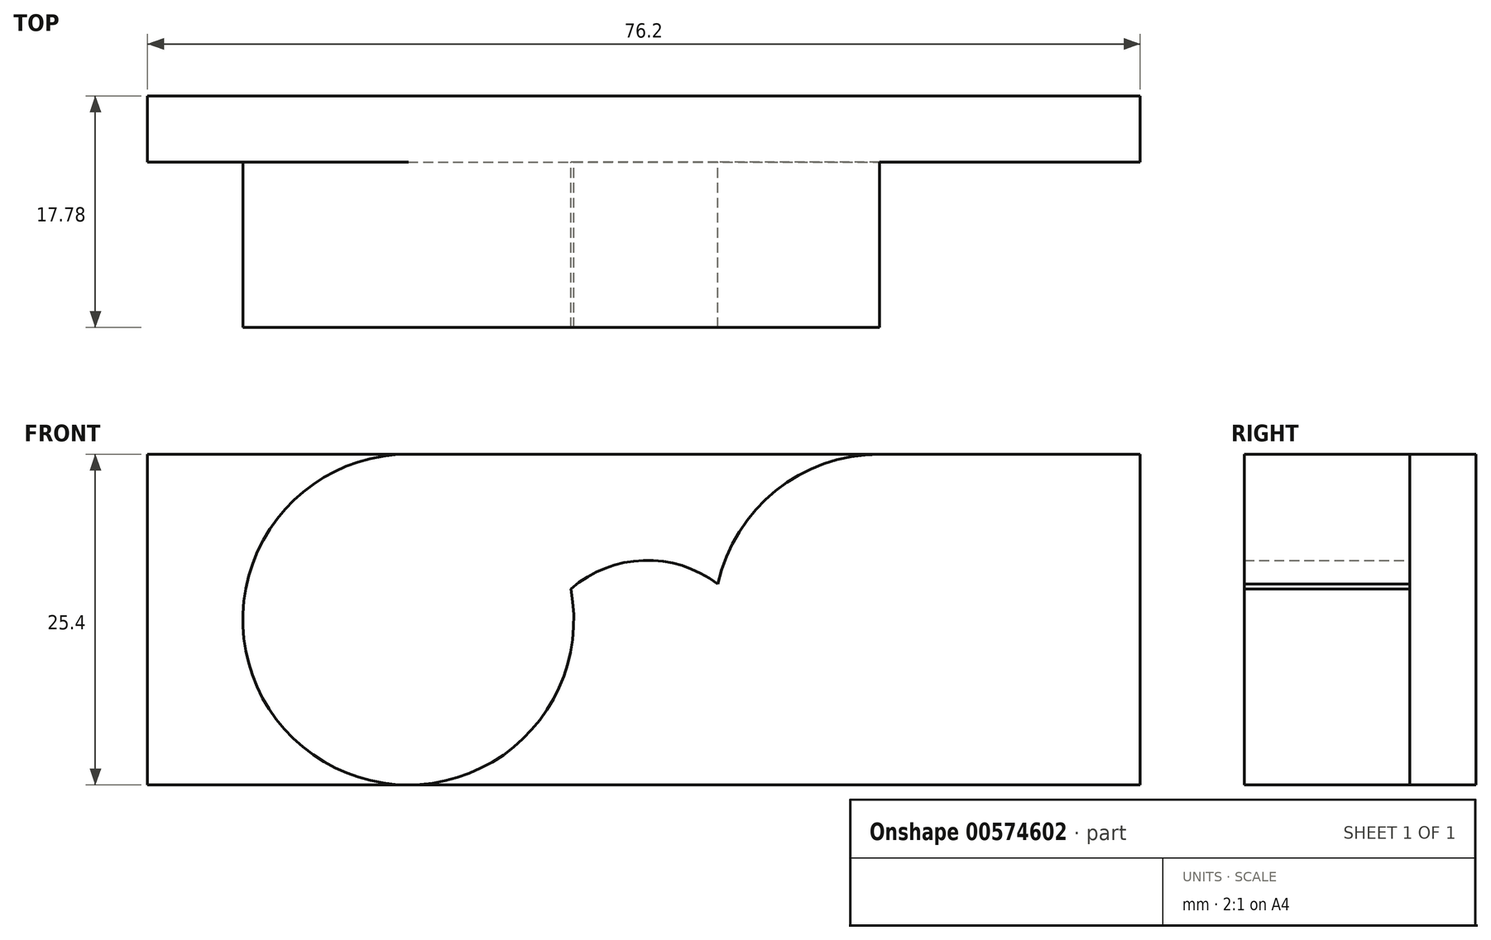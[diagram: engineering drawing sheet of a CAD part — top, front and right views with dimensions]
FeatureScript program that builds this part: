
annotation { "Feature Type Name" : "Feature", "Feature Type Description" : "" }
export const myFeature = defineFeature(function(context is Context, id is Id, definition is map)
    precondition{}
    {
        {
            var Q0;
            Q0=qCreatedBy(makeId("Front.planeOp"),FACE);
            var sketch = newSketch(context, id + "F0", { "sketchPlane" : qUnion([Q0])});
            skLineSegment(sketch, "E0.bottom", {"start": v(-38.1, 12.7) * mm, "end": v(38.1, 12.7) * mm});
            skLineSegment(sketch, "E0.top", {"start": v(-38.1, -12.7) * mm, "end": v(38.1, -12.7) * mm});
            skLineSegment(sketch, "E0.left", {"start": v(-38.1, 12.7) * mm, "end": v(-38.1, -12.7) * mm});
            skLineSegment(sketch, "E0.right", {"start": v(38.1, 12.7) * mm, "end": v(38.1, -12.7) * mm});
            skSolve(sketch);
        }
        {
            var Q0;
            Q0 = qSketchRegion(id + "F0", true);
            extrude(context, id + "F1", {"entities" : qUnion([Q0]), "depth" : 5.08 * mm, "offsetDistance" : 25.4 * mm});
        }
        {
            var Q0;
            Q0=makeQuery(id+"F1.opExtrude","CAP_FACE",FACE,{"disambiguationData":[OSD([sQuery(id+"F0.wireOp",EDGE,"E0.bottom"),sQuery(id+"F0.wireOp",EDGE,"E0.top"),sQuery(id+"F0.wireOp",EDGE,"E0.left"),sQuery(id+"F0.wireOp",EDGE,"E0.right")])],"isStart":false});
            var sketch = newSketch(context, id + "F2", { "sketchPlane" : qUnion([Q0])});
            skCircle(sketch, "E1", {"center": v(-18.08, 0) * mm, "radius": 12.7 * mm});
            skCircle(sketch, "E2.MirrorC", {"center": v(18.08, 0) * mm, "radius": 12.7 * mm});
            skArc(sketch, "E3", {"start": v(6.12, 4.27) * mm, "mid": v(0, 6.38) * mm, "end": v(-6.02, 3.98) * mm});
            skArc(sketch, "E4", {"start": v(5.68, 2.74) * mm, "mid": v(-0.03, 4.55) * mm, "end": v(-5.6, 2.36) * mm});
            skSolve(sketch);
        }
        {
            var Q0;
            {var subQ0=sQuery(id+"F2.wireOp",EDGE,"E1");var subQ1=makeQuery(id+"F2.imprint","INTERSECT",VERTEX,{"derivedFrom":[subQ0,sQuery(id+"F2.wireOp",EDGE,"E3")]});Q0=makeQuery(id+"F2.imprint","IMPRINT",FACE,{"disambiguationData":[TD([[makeQuery(id+"F2.imprint","IMPRINT",EDGE,{"disambiguationData":[TD([[subQ1,1.0]])],"derivedFrom":subQ0}),1.0]])]});}
            var Q1;
            {var subQ0=sQuery(id+"F2.wireOp",EDGE,"E3");Q1=makeQuery(id+"F2.imprint","IMPRINT",FACE,{"disambiguationData":[TD([[makeQuery(id+"F2.imprint","IMPRINT",EDGE,{"derivedFrom":subQ0}),1.0]])]});}
            var Q2;
            {var subQ0=sQuery(id+"F2.wireOp",EDGE,"E2.MirrorC");var subQ1=makeQuery(id+"F2.imprint","INTERSECT",VERTEX,{"derivedFrom":[subQ0,sQuery(id+"F2.wireOp",EDGE,"E3")]});Q2=makeQuery(id+"F2.imprint","IMPRINT",FACE,{"disambiguationData":[TD([[makeQuery(id+"F2.imprint","IMPRINT",EDGE,{"disambiguationData":[TD([[subQ1,1.0]])],"derivedFrom":subQ0}),-1.0]])]});}
            extrude(context, id + "F3", {"entities" : qUnion([Q0, Q1, Q2]), "operationType" : NewBodyOperationType.ADD, "depth" : 12.7 * mm, "offsetDistance" : 25.4 * mm});
        }
    });
